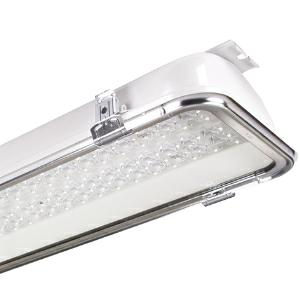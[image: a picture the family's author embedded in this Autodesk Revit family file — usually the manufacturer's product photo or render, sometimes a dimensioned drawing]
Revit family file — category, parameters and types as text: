
# Revit family: 3f_filippi_-_beta_235_76_vt_ampio_3f_filippi_-_52769_-_beta_235_led_762x55_ampio_vt_l1565
name_source: partatom
category: Lighting Fixtures
units: mm (PartAtom-declared; Revit-internal decimal feet)

## family parameters
Cut with Voids When Loaded = No
Host = Face
Light Source = No
Part Type = Normal
Room Calculation Point = No
Round Connector Dimension = Use Diameter
Shared = No

## types (1)
- 3F Filippi - Beta 235 76 VT Ampio (1 x LED, 18085 lm, 112 W, 4000 K)
    Apparent Load = 112 VA
    Approval mark = CE
    CIE Flux Codes = 55 92 99 100 100
    Color Rendering = 80
    Color Temperature = 4000 K
    Control Gear = Electronic ballast
    Default Elevation = 1800 mm
    Description = ILLUMINOTECHNICAL
Luminous efficiency 100% (DLOR 100%, ULOR 0%).
Initial luminous flux of the luminaire 18085 lm.
Wide symmetric distribution.
Installation Interdistance Transv.D = 1.18 x hu - Long.D = 1.19 x hu.
Tabular UGR (CIE 117 - 4H-8H; S=0.25H; 70/50/20): RUG 22.2 - 23.9.
Beam angle: 100° - 106°.
Luminous efficacy 161 lm/W.
Lifetime (L93/B10): 30000 h. (tq+25°C)
Lifetime (L90/B10): 50000 h. (tq+25°C)
Lifetime (L85/B10): 80000 h. (tq+25°C)
Lifetime (L80/B10): 100000 h. (tq+25°C)
Lifetime (L85/B10): 50000 h. (tq+45°C)
Sudden decreased luminous flux after 50000 hours: 0% (C0).
Photobiological safety in compliance with IEC/TR 62778: RG0 risk exempt, (IEC 62471).
In compliance with IEC/EN 62722-2-1 - IEC/EN 62717 standards.

SOURCE
2 linear LED modules 55W/840.
Energy efficiency class (UE 2019/2020 - UE 2019/2015): C.
CIE 13.3 Colour rendering index: CRI >80 (R9 <50%).
IES TM-30 Fidelity Index: Rf = 84 Rg = 95.
CCT nominal colour temperature 4000 K.
Colour initial tolerance (MacAdam): SDCM 3.

MECHANICAL
Single-piece housing in pressed steel, powder-coated in white epoxy-polyester.
VT transparent glass, non-combustible, single-piece perimeter frame in galvanised steel.
Ecologic anti-aging injected sealing gasket.
Oversized gear-tray reflector unit in highly reflective white painted hot-galvanised steel.
Methacrylate (PMMA) lenses with external flat surface.
Galvanised steel snap-lock clips for diffuser mounting (safety n° 4 per fixture).
Luminaire with limited surface temperature. - D - (EN 60598-2-24)
Dimensions: 1565x235 mm, height 105 mm. Weight 12.175 kg.
IP66 protection degree.
Mechanical strength to impacts IK09 (10 joule).
Glow-wire test resistance 960°C.

ELECTRICAL
Halogen Free electronic wiring 230V-50/60Hz, power factor 0.95, THD <25%, constant output current, class I, 1 driver.
Power of the luminaire 112 W.
ENEC - CE.
SAFE FLICKER: PstLM=<1 and SVM=<0.4 (IEC TR 61547-1 and IEC TR 63158), to ensure a more comfortable and safe light.
Luminaire compliant with EN 60598-2-22 for power supply from a centralised emergency system CPSS (Central Power Supply System), not incorporated in the luminaire - high risk areas excluded. The default power and flux are 100% in AC and 100% in DC.
Ambient temperature from -20°C to +45°C.
Temperature class T6 max 85°C.
Quick connection via M20 3P connector with 9-13 mm tightening range.
Relative humidity UR: <85%.

INSTALLATION
Ceiling / Suspended / Wall.
All accessories dedicated to this product are available on the Catalog and on our website www.3F-Filippi.com.

APPLICATIONS
Dry, dusty indoor environments, subject to occasional water splashes.
Industrial environments, warehouses, environments where security locks are required on all clips, e.g. prisons (on request).
Environments in which it is necessary a total protection against falling fragments (eg environments with foodstuffs or machines with moving parts or with extreme temperature changes), use luminaires with laminated glass.
Tempered glass is not immune to falling fragments from harmless and caused by shocks or exceptionally derived from the tempering process.

WARNING
Fixture not suitable for cold stores with an ambient temperature <0°C and/or relative humidity >85%.
Luminaire designed for disposal/recycling at end-of-life.
Replaceable (LED only) light source by a professional. Replaceable control gear by a professional.
    Height = 105 mm
    Lamp = 1 x LED
    Lamp Light Flux = 18085 lm
    Lamp Power = 112 W
    Lamp count = 1
    Length = 1565 mm
    Lifetime = 50000 h
    Luminous efficacy = 161 lm/W
    Manufacturer = 3F Filippi
    ModVariant = No
    Model = 3F Filippi - 52769 - Beta 235 LED 762x55 AMPIO VT L1565
    Mounting Place = Ceiling
    Mounting Type = Pendant
    Number of Poles = 1
    OnlyDefault = Yes
    Power Factor = 1
    Product Name = 3F Filippi - Beta 235 76 VT Ampio
    Product group = pendant luminaire
    ProductGroupID = 9
    Protection Class = Protection class I
    Protection Degree = IP 66
    RLX_Detail_Level = 1
    RLX_Emergency_Light_Flux = 0 lm
    RLX_Emergency_Type = 0
    RLX_Emergency_Type_DB = No
    RlxData = <blob elided: 88405 chars, md5=c3f322ea>
    Socket = socket
    Standby Power = 0 W
    System Light Flux = 18085 lm
    System Power = 112 W
    Type Comments = Product without accessories
    Type Image = 3ffilippi_52769.jpg
    URL = http://relux.com
    VarID = ---
    Voltage = 0 V
    Weight = 0.00 kg
    Width = 235 mm

## geometry (parser evidence)
native form markers: Blend x4, Sweep x12
no freeform markers — native parametric forms only
